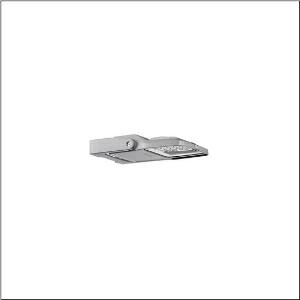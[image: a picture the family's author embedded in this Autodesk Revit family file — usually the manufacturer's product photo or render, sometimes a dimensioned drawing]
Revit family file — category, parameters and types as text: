
# Revit family: floodlight_fl_21_iq_micro___pl64_5xa7761a2e2a_9d46
name_source: partatom
category: Lighting Fixtures
units: mm (PartAtom-declared; Revit-internal decimal feet)

## family parameters
Cut with Voids When Loaded = No
Host = Face
Light Source = No
Part Type = Normal
Room Calculation Point = No
Round Connector Dimension = Use Diameter
Shared = No

## types (1)
- --- (1 x LED, 2870 lm, 23.1 W, 3000K)
    Apparent Load = 23 VA
    CIE Flux Codes = 28 80 98 100 100
    Color Rendering = 70
    Color Temperature = 3000K
    Default Elevation = 1800 mm
    Description = Floodlight FL 21 iQ micro, floodlight, primary light control with lens, of PMMA, primary optical cover: protective disc, of toughened safety glass, transparent, light distribution: PL64, light emission: direct distribution, installation type: surface-mounted, LED, High Power LED, rated luminous flux: 2.870lm, luminous efficacy: 124lm/W, light colour: 730, colour temperature: 3000K, control: optimised constant luminous flux control (CLO 2.0), Desk-Remote (wireless, voltage-free reading and setting of iQ features in the workshop via application-optimized NFC function/RFID function), Light-Fading, Smart-Wire, Night-Set, Lumen-Switch, Temp-Guard, Auto-Match, with terminal, 6-pole, mains connection: 220..240V, AC, 50/60Hz, start of lifetime: 23W, end of service life: 24W, reduction: 11W, luminaire housing, of diecast aluminium, powder-coated, Siteco® metallic grey (DB 702S), corrosivity category C5 mid according to DIN EN ISO 12944, sealing non-destructively replaceable, design bracket, of diecast aluminium, powder-coated, Siteco® metallic grey (DB 702S), protection rating (complete): IP66, insulation class (complete): insulation class II (safety insulation), certification: CE, ENEC, VDE, protection symbol: D, impact resistance: IK07, permissible operating ambient temperature: -40..+40°C, permissible operating ambient temperature for outdoor applications: -40..+50°C, standard: DIN EN 12944, LABS conformity tested according to VDMA 24364:2018-05, packaging unit: 1 piece

Light Distribution: PL64
    Height = 65 mm
    Lamp = 1 x LED
    Lamp Light Flux = 2870 lm
    Lamp Power = 23.1 W
    Lamp count = 1
    Length = 312 mm
    Luminous efficacy = 124 lm/W
    Manufacturer = Siteco
    ModVariant = No
    Model = 5XA7761A2E2A
    Mounting Place = Wall
    Mounting Type = Surface mounted
    Number of Poles = 1
    OnlyDefault = Yes
    Power Factor = 1
    Product Name = Floodlight FL 21 iQ micro | PL64
    Product group = floodlight | wall mounted
    ProductGroupID = 2001
    Protection Class = Protection class II
    Protection Degree = IP 66
    RLX_Detail_Level = 1
    RLX_Emergency_Light_Flux = 0 lm
    RLX_Emergency_Type = 0
    RLX_Emergency_Type_DB = No
    RlxData = <blob elided: 97377 chars, md5=46fbe504>
    Socket = socket
    Standby Power = 0 W
    System Light Flux = 2870 lm
    System Power = 23 W
    Type Comments = factory setting: luminous flux: 100 % | dim-lin: 254 | 455 mA
    Type Image = l_1006878.jpg
    URL = http://relux.com
    VarID = @adj_113971
    Voltage = 0 V
    Weight = 0.00 kg
    Width = 230 mm

## geometry (parser evidence)
native form markers: Blend x4, Sweep x13
no freeform markers — native parametric forms only
